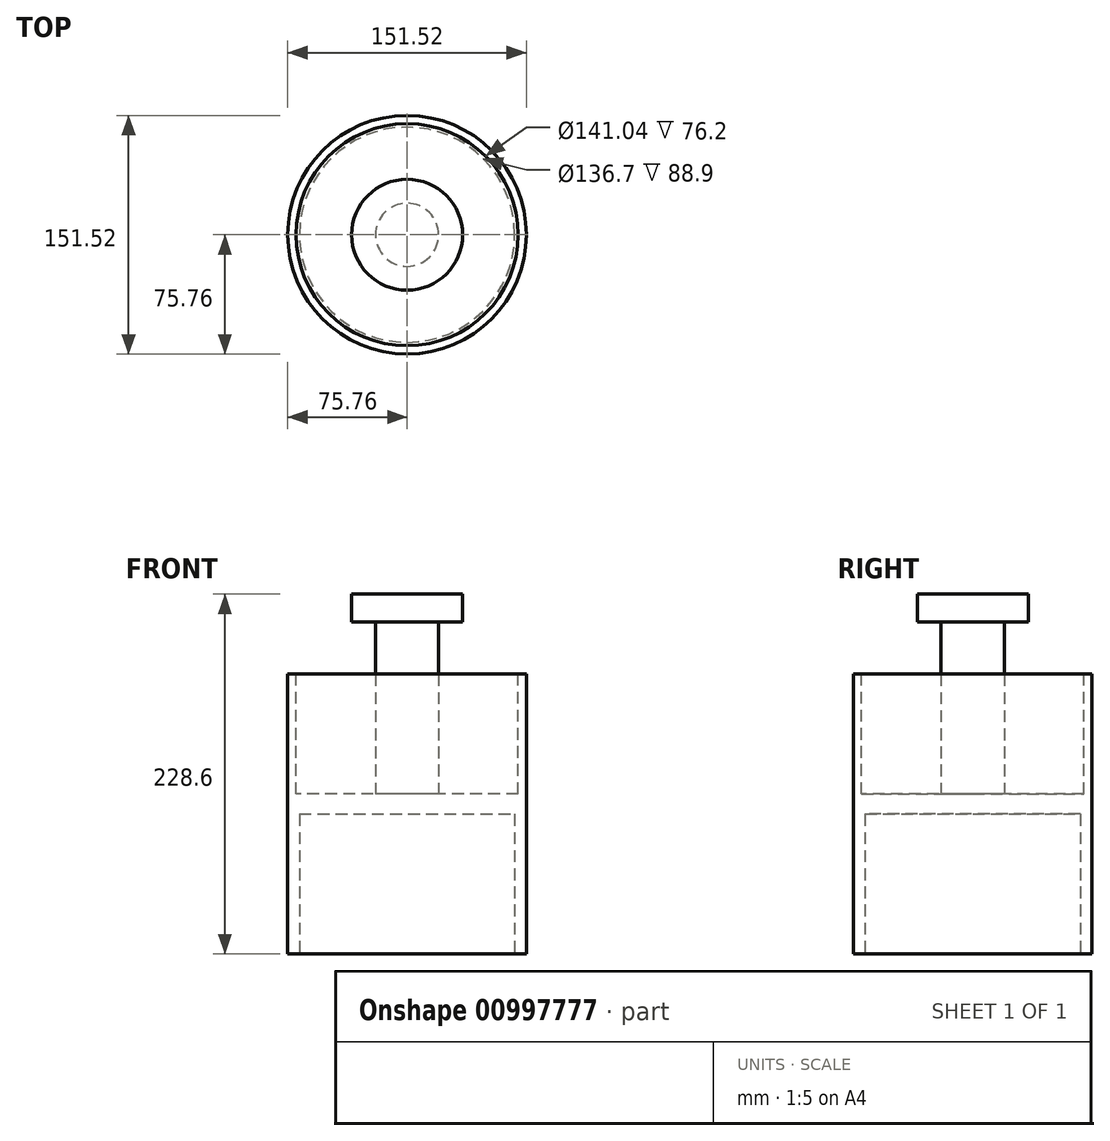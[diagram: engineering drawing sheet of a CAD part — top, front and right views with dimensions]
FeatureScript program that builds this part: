
annotation { "Feature Type Name" : "Feature", "Feature Type Description" : "" }
export const myFeature = defineFeature(function(context is Context, id is Id, definition is map)
    precondition{}
    {
        {
            var Q0;
            Q0=qCreatedBy(makeId("Top.planeOp"),FACE);
            var sketch = newSketch(context, id + "F0", { "sketchPlane" : qUnion([Q0])});
            skCircle(sketch, "E0", {"center": v(0, 0) * mm, "radius": 75.76 * mm});
            skSolve(sketch);
        }
        {
            var Q0;
            Q0=makeQuery(id+"F0.imprint","IMPRINT",FACE,{"disambiguationData":[TD([[makeQuery(id+"F0.imprint","IMPRINT",EDGE,{"derivedFrom":sQuery(id+"F0.wireOp",EDGE,"E0")}),1.0]])]});
            extrude(context, id + "F1", {"entities" : qUnion([Q0]), "depth" : 177.8 * mm, "offsetDistance" : 25.4 * mm});
        }
        {
            var Q0;
            Q0=makeQuery(id+"F1.opExtrude","CAP_FACE",FACE,{"disambiguationData":[OSD([sQuery(id+"F0.wireOp",EDGE,"E0")])],"isStart":false});
            var sketch = newSketch(context, id + "F2", { "sketchPlane" : qUnion([Q0])});
            skCircle(sketch, "E1", {"center": v(0, 0) * mm, "radius": 70.52 * mm});
            skSolve(sketch);
        }
        {
            var Q0;
            Q0=makeQuery(id+"F2.imprint","IMPRINT",FACE,{"disambiguationData":[TD([[makeQuery(id+"F2.imprint","IMPRINT",EDGE,{"derivedFrom":sQuery(id+"F2.wireOp",EDGE,"E1")}),1.0]])]});
            extrude(context, id + "F3", {"entities" : qUnion([Q0]), "operationType" : NewBodyOperationType.REMOVE, "depth" : -76.2 * mm, "offsetDistance" : 25.4 * mm});
        }
        {
            var Q0;
            Q0=makeQuery(id+"F3.boolean.opBoolean","COPY",FACE,{"derivedFrom":makeQuery(id+"F3.opExtrude","CAP_FACE",FACE,{"disambiguationData":[OSD([sQuery(id+"F2.wireOp",EDGE,"E1")])],"isStart":false})});
            var sketch = newSketch(context, id + "F4", { "sketchPlane" : qUnion([Q0])});
            skCircle(sketch, "E2", {"center": v(0, 0) * mm, "radius": 20.05 * mm});
            skSolve(sketch);
        }
        {
            var Q0;
            Q0=makeQuery(id+"F4.imprint","IMPRINT",FACE,{"disambiguationData":[TD([[makeQuery(id+"F4.imprint","IMPRINT",EDGE,{"derivedFrom":sQuery(id+"F4.wireOp",EDGE,"E2")}),1.0]])]});
            extrude(context, id + "F5", {"entities" : qUnion([Q0]), "operationType" : NewBodyOperationType.ADD, "depth" : 127 * mm, "offsetDistance" : 25.4 * mm});
        }
        {
            var Q0;
            Q0=makeQuery(id+"F5.opExtrude","CAP_FACE",FACE,{"disambiguationData":[OSD([sQuery(id+"F4.wireOp",EDGE,"E2")])],"isStart":false});
            var sketch = newSketch(context, id + "F6", { "sketchPlane" : qUnion([Q0])});
            skCircle(sketch, "E3", {"center": v(0, 0) * mm, "radius": 35.25 * mm});
            skSolve(sketch);
        }
        {
            var Q0;
            Q0=makeQuery(id+"F6.imprint","IMPRINT",FACE,{"disambiguationData":[TD([[makeQuery(id+"F6.imprint","IMPRINT",EDGE,{"derivedFrom":sQuery(id+"F6.wireOp",EDGE,"E3")}),1.0]])]});
            extrude(context, id + "F7", {"entities" : qUnion([Q0]), "operationType" : NewBodyOperationType.ADD, "oppositeDirection" : true, "depth" : 17.78 * mm, "offsetDistance" : 25.4 * mm});
        }
        {
            var Q0;
            Q0=makeQuery(id+"F1.opExtrude","CAP_FACE",FACE,{"disambiguationData":[OSD([sQuery(id+"F0.wireOp",EDGE,"E0")])],"isStart":true});
            var sketch = newSketch(context, id + "F8", { "sketchPlane" : qUnion([Q0])});
            skCircle(sketch, "E4", {"center": v(0, 0) * mm, "radius": 68.35 * mm});
            skSolve(sketch);
        }
        {
            var Q0;
            Q0=makeQuery(id+"F8.imprint","IMPRINT",FACE,{"disambiguationData":[TD([[makeQuery(id+"F8.imprint","IMPRINT",EDGE,{"derivedFrom":sQuery(id+"F8.wireOp",EDGE,"E4")}),1.0]])]});
            extrude(context, id + "F9", {"entities" : qUnion([Q0]), "operationType" : NewBodyOperationType.REMOVE, "oppositeDirection" : true, "depth" : 88.9 * mm, "offsetDistance" : 25.4 * mm});
        }
    });
